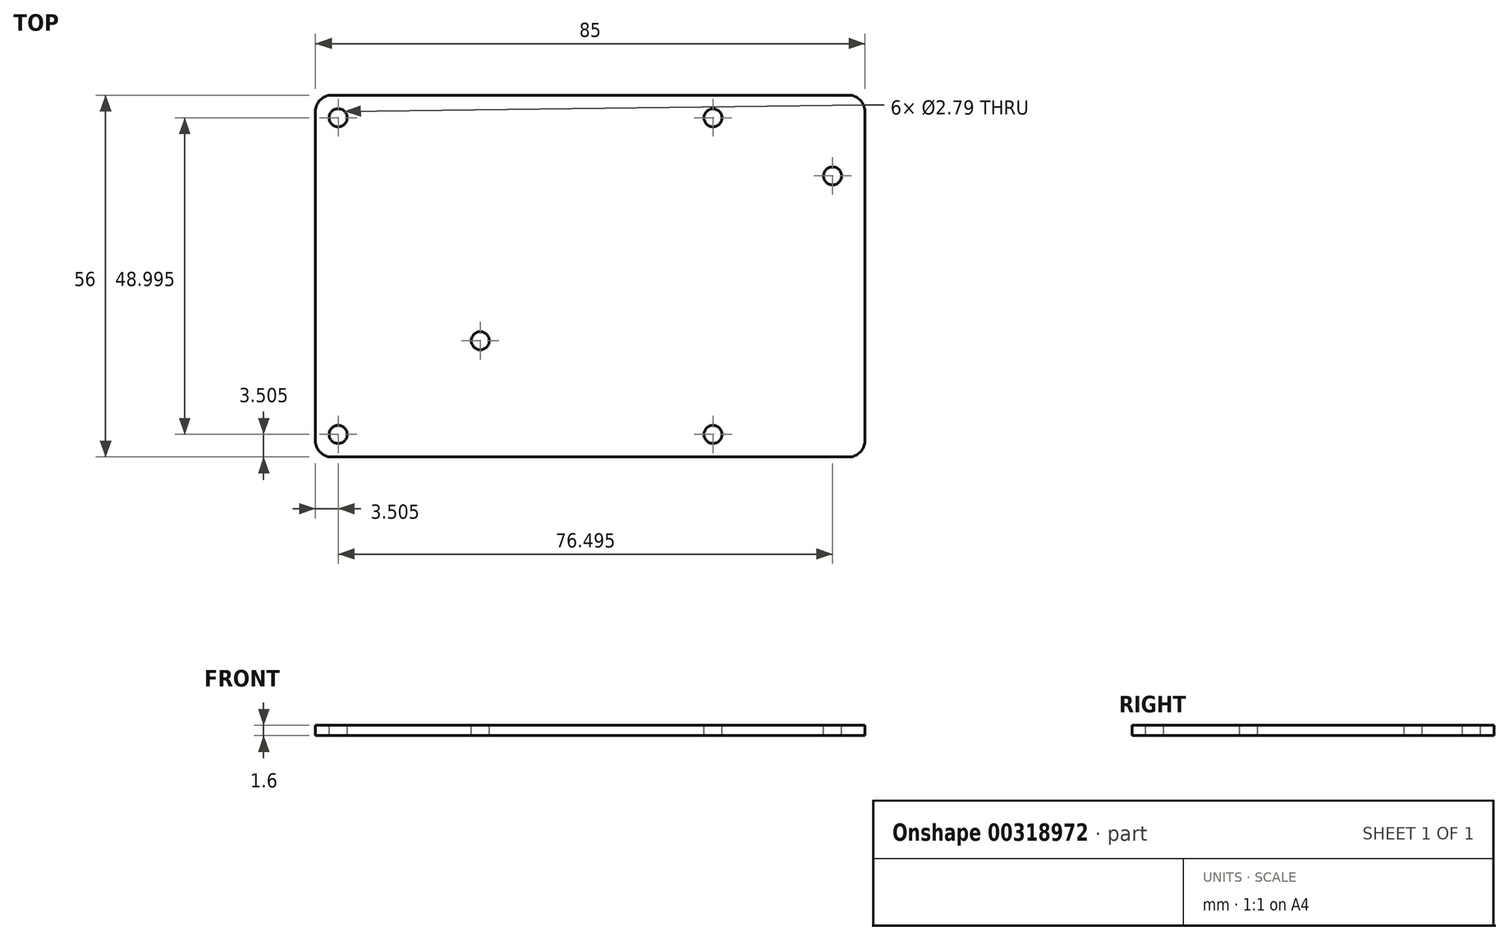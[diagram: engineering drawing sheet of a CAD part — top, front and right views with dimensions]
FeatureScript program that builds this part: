
annotation { "Feature Type Name" : "Feature", "Feature Type Description" : "" }
export const myFeature = defineFeature(function(context is Context, id is Id, definition is map)
    precondition{}
    {
        {
            var Q0;
            Q0=qCreatedBy(makeId("Top.planeOp"),FACE);
            var sketch = newSketch(context, id + "F0", { "sketchPlane" : qUnion([Q0])});
            skLineSegment(sketch, "E0.bottom", {"start": v(42.5, 28) * mm, "end": v(-42.5, 28) * mm});
            skLineSegment(sketch, "E0.top", {"start": v(42.5, -28) * mm, "end": v(-42.5, -28) * mm});
            skLineSegment(sketch, "E0.left", {"start": v(42.5, 28) * mm, "end": v(42.5, -28) * mm});
            skLineSegment(sketch, "E0.right", {"start": v(-42.5, 28) * mm, "end": v(-42.5, -28) * mm});
            skPoint(sketch, "E0.middle", {"position": v(0, 0) * mm});
            skSolve(sketch);
        }
        {
            var Q0;
            Q0=makeQuery(id+"F0.imprint","IMPRINT",FACE,{"disambiguationData":[TD([[makeQuery(id+"F0.imprint","IMPRINT",EDGE,{"derivedFrom":sQuery(id+"F0.wireOp",EDGE,"E0.bottom")}),1.0]])]});
            extrude(context, id + "F1", {"entities" : qUnion([Q0]), "depth" : 1.6 * mm});
        }
        {
            var Q0;
            Q0=makeQuery(id+"F1.opExtrude","CAP_FACE",FACE,{"disambiguationData":[OSD([sQuery(id+"F0.wireOp",EDGE,"E0.bottom"),sQuery(id+"F0.wireOp",EDGE,"E0.top"),sQuery(id+"F0.wireOp",EDGE,"E0.left"),sQuery(id+"F0.wireOp",EDGE,"E0.right")])],"isStart":false});
            var sketch = newSketch(context, id + "F2", { "sketchPlane" : qUnion([Q0])});
            skCircle(sketch, "E1", {"center": v(-39, 24.5) * mm, "radius": 1.4 * mm});
            skCircle(sketch, "E2", {"center": v(-39, -24.5) * mm, "radius": 1.4 * mm});
            skCircle(sketch, "E3", {"center": v(19, 24.5) * mm, "radius": 1.4 * mm});
            skCircle(sketch, "E4", {"center": v(19, -24.5) * mm, "radius": 1.4 * mm});
            skSolve(sketch);
        }
        {
            var Q0;
            Q0 = qSketchRegion(id + "F2", true);
            extrude(context, id + "F3", {"entities" : qUnion([Q0]), "operationType" : NewBodyOperationType.REMOVE, "oppositeDirection" : true, "depth" : 25.4 * mm});
        }
        {
            var Q0;
            Q0=makeQuery(id+"F1.opExtrude","CAP_FACE",FACE,{"disambiguationData":[OSD([sQuery(id+"F0.wireOp",EDGE,"E0.bottom"),sQuery(id+"F0.wireOp",EDGE,"E0.top"),sQuery(id+"F0.wireOp",EDGE,"E0.left"),sQuery(id+"F0.wireOp",EDGE,"E0.right")])],"isStart":false});
            var sketch = newSketch(context, id + "F4", { "sketchPlane" : qUnion([Q0])});
            skCircle(sketch, "E5", {"center": v(-17, -10) * mm, "radius": 1.4 * mm});
            skCircle(sketch, "E6", {"center": v(37.5, 15.5) * mm, "radius": 1.4 * mm});
            skSolve(sketch);
        }
        {
            var Q0;
            Q0 = qSketchRegion(id + "F4", true);
            extrude(context, id + "F5", {"entities" : qUnion([Q0]), "operationType" : NewBodyOperationType.REMOVE, "oppositeDirection" : true, "depth" : 25.4 * mm});
        }
        {
            var Q0;
            Q0=makeQuery(id+"F1.opExtrude","SWEPT_EDGE",EDGE,{"disambiguationData":[OSD([sQuery(id+"F0.wireOp",EDGE,"E0.top"),sQuery(id+"F0.wireOp",EDGE,"E0.right")])]});
            var Q1;
            Q1=makeQuery(id+"F1.opExtrude","SWEPT_EDGE",EDGE,{"disambiguationData":[OSD([sQuery(id+"F0.wireOp",EDGE,"E0.top"),sQuery(id+"F0.wireOp",EDGE,"E0.left")])]});
            var Q2;
            Q2=makeQuery(id+"F1.opExtrude","SWEPT_EDGE",EDGE,{"disambiguationData":[OSD([sQuery(id+"F0.wireOp",EDGE,"E0.bottom"),sQuery(id+"F0.wireOp",EDGE,"E0.left")])]});
            var Q3;
            Q3=makeQuery(id+"F1.opExtrude","SWEPT_EDGE",EDGE,{"disambiguationData":[OSD([sQuery(id+"F0.wireOp",EDGE,"E0.bottom"),sQuery(id+"F0.wireOp",EDGE,"E0.right")])]});
            fillet(context, id + "F6", {"entities" : qUnion([Q0, Q1, Q2, Q3]), "radius" : 2.54 * mm, "tangentPropagation" : true, "allowEdgeOverflow" : false});
        }
    });
